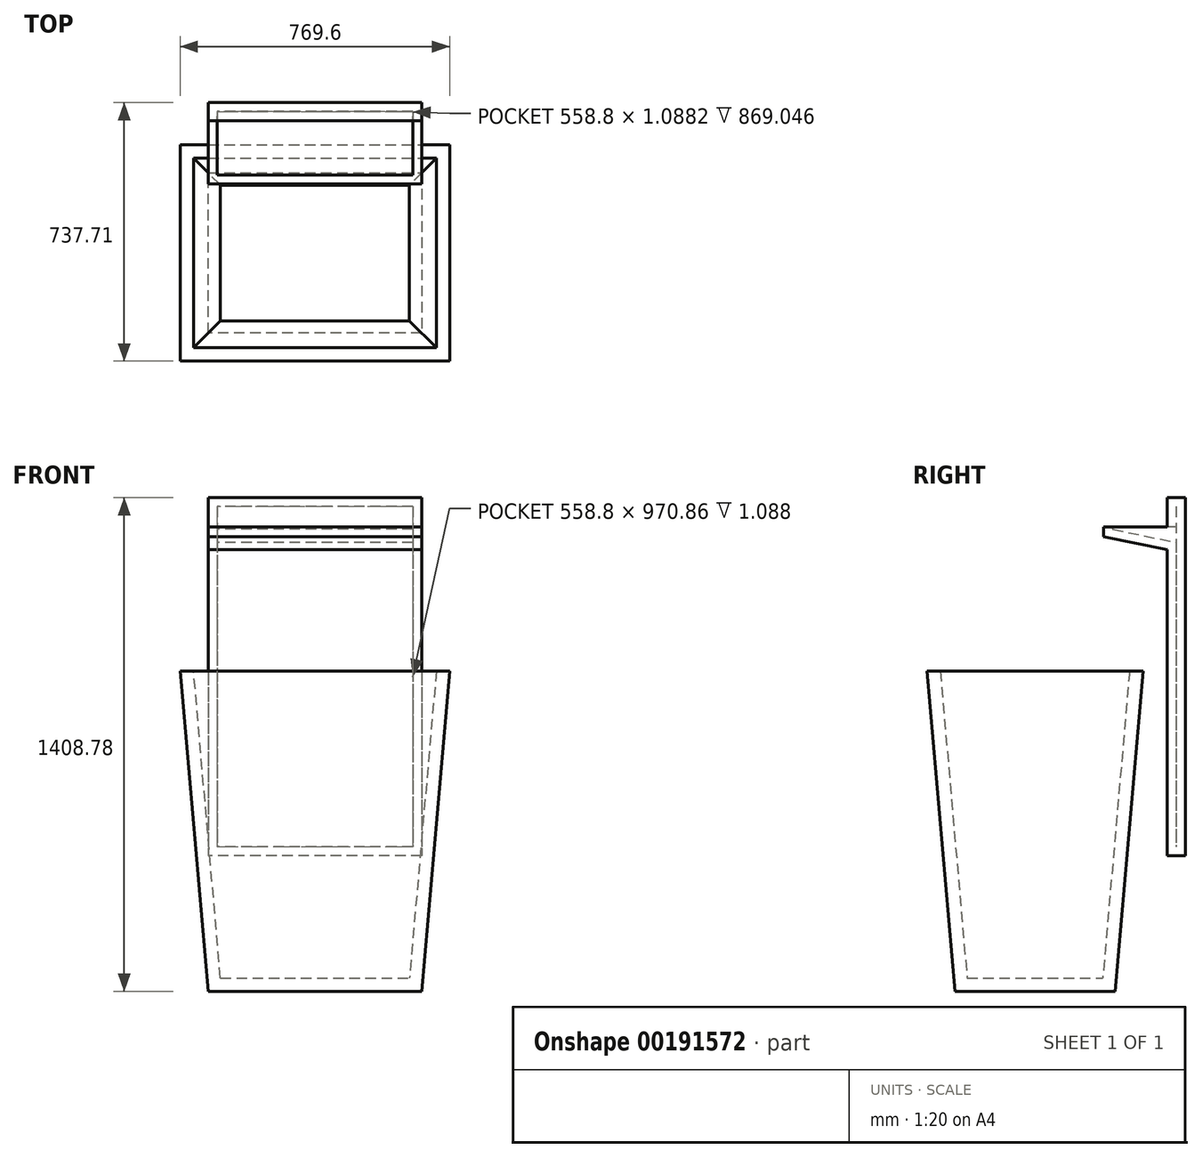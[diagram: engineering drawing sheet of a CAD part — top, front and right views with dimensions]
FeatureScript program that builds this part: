
annotation { "Feature Type Name" : "Feature", "Feature Type Description" : "" }
export const myFeature = defineFeature(function(context is Context, id is Id, definition is map)
    precondition{}
    {
        {
            var Q0;
            Q0=qCreatedBy(makeId("Top.planeOp"),FACE);
            var sketch = newSketch(context, id + "F0", { "sketchPlane" : qUnion([Q0])});
            skLineSegment(sketch, "E0.bottom", {"start": v(0, 0) * mm, "end": v(609.6, 0) * mm});
            skLineSegment(sketch, "E0.top", {"start": v(0, -457.2) * mm, "end": v(609.6, -457.2) * mm});
            skLineSegment(sketch, "E0.left", {"start": v(0, 0) * mm, "end": v(0, -457.2) * mm});
            skLineSegment(sketch, "E0.right", {"start": v(609.6, 0) * mm, "end": v(609.6, -457.2) * mm});
            skSolve(sketch);
        }
        {
            var Q0;
            Q0 = qSketchRegion(id + "F0", true);
            extrude(context, id + "F1", {"entities" : qUnion([Q0]), "depth" : 914.4 * mm, "hasDraft" : true, "draftAngle" : 5 * degree});
        }
        {
            var Q0;
            Q0=makeQuery(id+"F1.opExtrude","CAP_FACE",FACE,{"disambiguationData":[OSD([sQuery(id+"F0.wireOp",EDGE,"E0.bottom"),sQuery(id+"F0.wireOp",EDGE,"E0.top"),sQuery(id+"F0.wireOp",EDGE,"E0.left"),sQuery(id+"F0.wireOp",EDGE,"E0.right")])],"isStart":false});
            shell(context, id + "F2", {"entities" : qUnion([Q0]), "thickness" : 38.1 * mm});
        }
        {
            var Q0;
            Q0=qCreatedBy(makeId("Right.planeOp"),FACE);
            var sketch = newSketch(context, id + "F3", { "sketchPlane" : qUnion([Q0])});
            skLineSegment(sketch, "E1.bottom", {"start": v(581.5, 519.78) * mm, "end": v(529.62, 519.78) * mm});
            skLineSegment(sketch, "E1.top", {"start": v(581.5, -501.88) * mm, "end": v(529.62, -501.88) * mm});
            skLineSegment(sketch, "E1.left", {"start": v(581.5, 519.78) * mm, "end": v(581.5, -501.88) * mm});
            skLineSegment(sketch, "E1.right", {"start": v(529.62, 519.78) * mm, "end": v(529.62, -501.88) * mm});
            skLineSegment(sketch, "E2", {"start": v(529.62, 436.4) * mm, "end": v(348.96, 436.4) * mm});
            skLineSegment(sketch, "E3", {"start": v(348.96, 436.4) * mm, "end": v(348.96, 408.99) * mm});
            skLineSegment(sketch, "E4", {"start": v(348.96, 408.99) * mm, "end": v(529.62, 371.85) * mm});
            skSolve(sketch);
        }
        {
            var Q0;
            {var subQ1=sQuery(id+"F3.wireOp",EDGE,"E1.bottom");Q0=makeQuery(id+"F3.imprint","IMPRINT",FACE,{"disambiguationData":[TD([[makeQuery(id+"F3.imprint","IMPRINT",EDGE,{"derivedFrom":subQ1}),1.0]])]});}
            extrude(context, id + "F4", {"entities" : qUnion([Q0]), "depth" : 304.8 * mm});
        }
        {
            var Q0;
            Q0 = qSketchRegion(id + "F3", true);
            extrude(context, id + "F5", {"entities" : qUnion([Q0]), "operationType" : NewBodyOperationType.ADD, "depth" : 609.6 * mm});
        }
        {
            var Q0;
            Q0=makeQuery(id+"F5.opExtrude","SWEPT_FACE",FACE,{"disambiguationData":[OSD([sQuery(id+"F3.wireOp",EDGE,"E2")])]});
            shell(context, id + "F6", {"entities" : qUnion([Q0]), "thickness" : 25.4 * mm});
        }
        {
            var Q0;
            Q0=makeQuery(id+"F4.opExtrude","SWEPT_BODY",BODY,{"disambiguationData":[OSD([sQuery(id+"F3.wireOp",EDGE,"E1.bottom"),sQuery(id+"F3.wireOp",EDGE,"E1.top"),sQuery(id+"F3.wireOp",EDGE,"E1.left"),sQuery(id+"F3.wireOp",EDGE,"E1.right")])]});
            var Q1;
            Q1=makeQuery(id+"F4.opExtrude","CAP_VERTEX",VERTEX,{"disambiguationData":[OSD([sQuery(id+"F3.wireOp",EDGE,"E1.top"),sQuery(id+"F3.wireOp",EDGE,"E1.right")])],"isStart":false});
            var Q2;
            Q2=qCreatedBy(makeId("Top.planeOp"),FACE);
            transform(context, id + "F7", {"entities" : qUnion([Q0]), "transformType" : TransformType.TRANSLATION_DISTANCE, "transformDirection" : qUnion([Q1, Q2]), "distance" : 508 * mm, "makeCopy" : false});
        }
        {
            var Q0;
            Q0=makeQuery(id+"F4.opExtrude","SWEPT_BODY",BODY,{"disambiguationData":[OSD([sQuery(id+"F3.wireOp",EDGE,"E1.bottom"),sQuery(id+"F3.wireOp",EDGE,"E1.top"),sQuery(id+"F3.wireOp",EDGE,"E1.left"),sQuery(id+"F3.wireOp",EDGE,"E1.right")])]});
            transform(context, id + "F8", {"entities" : qUnion([Q0]), "transformType" : TransformType.TRANSLATION_3D, "dx" : 0 * mm, "dy" : 0 * mm, "dz" : 381 * mm, "makeCopy" : false});
        }
        {
            var Q0;
            Q0=makeQuery(id+"F4.opExtrude","SWEPT_BODY",BODY,{"disambiguationData":[OSD([sQuery(id+"F3.wireOp",EDGE,"E1.bottom"),sQuery(id+"F3.wireOp",EDGE,"E1.top"),sQuery(id+"F3.wireOp",EDGE,"E1.left"),sQuery(id+"F3.wireOp",EDGE,"E1.right")])]});
            transform(context, id + "F9", {"entities" : qUnion([Q0]), "transformType" : TransformType.TRANSLATION_3D, "dx" : 0 * mm, "dy" : -381 * mm, "dz" : 0 * mm, "makeCopy" : false});
        }
        {
            var Q0;
            Q0=makeQuery(id+"F4.opExtrude","SWEPT_BODY",BODY,{"disambiguationData":[OSD([sQuery(id+"F3.wireOp",EDGE,"E1.bottom"),sQuery(id+"F3.wireOp",EDGE,"E1.top"),sQuery(id+"F3.wireOp",EDGE,"E1.left"),sQuery(id+"F3.wireOp",EDGE,"E1.right")])]});
            transform(context, id + "F10", {"entities" : qUnion([Q0]), "transformType" : TransformType.TRANSLATION_3D, "dx" : 0 * mm, "dy" : 0 * mm, "dz" : 0 * mm, "makeCopy" : true});
        }
    });
